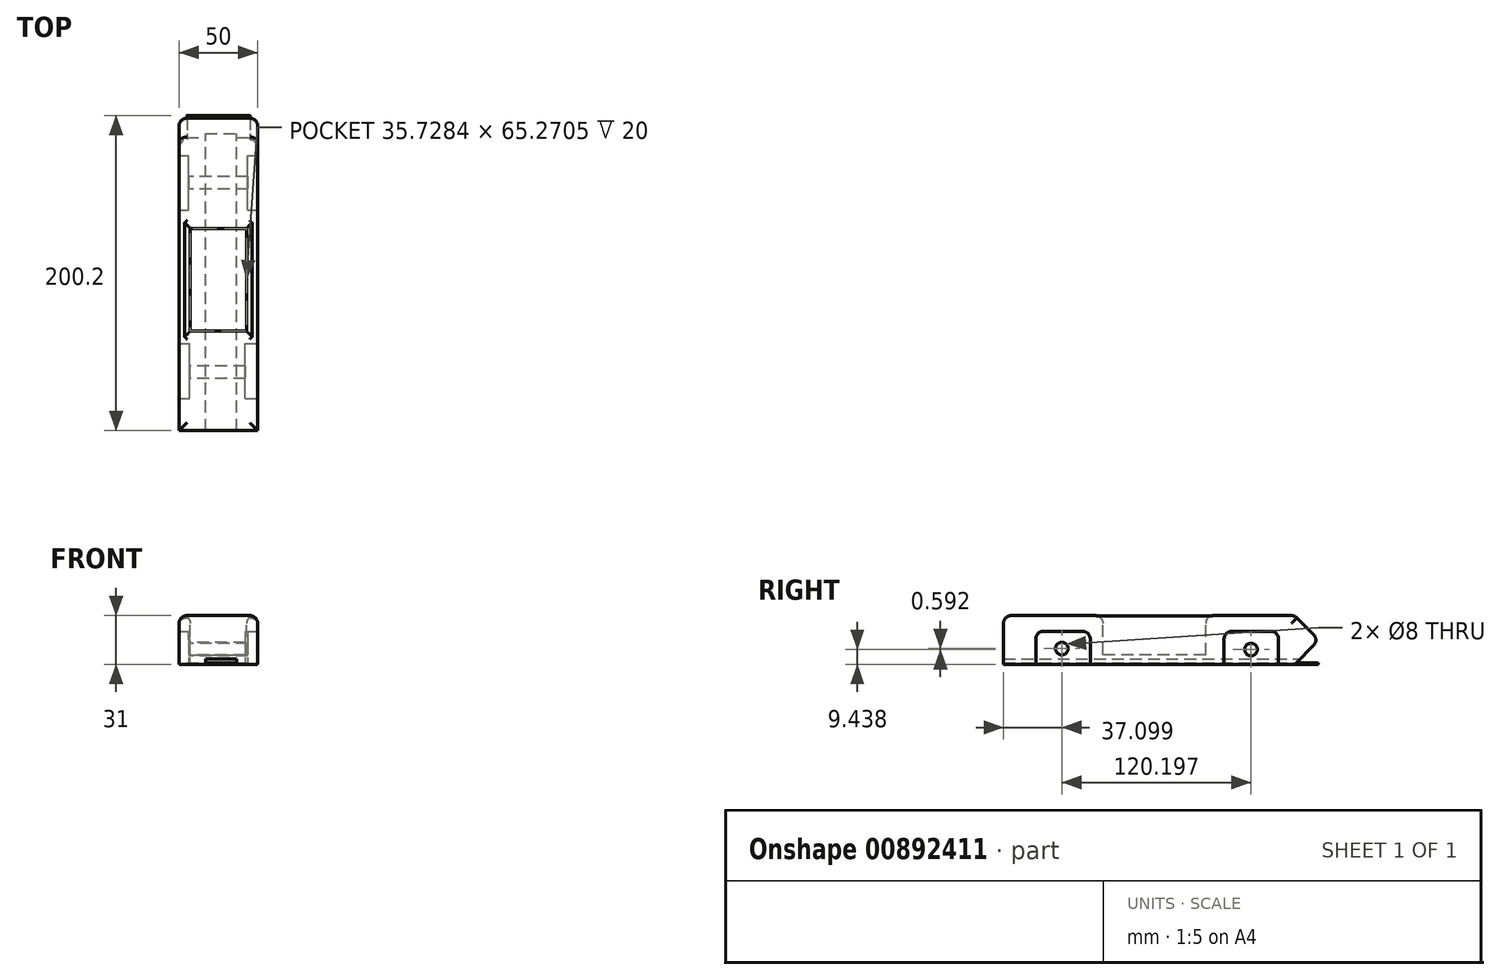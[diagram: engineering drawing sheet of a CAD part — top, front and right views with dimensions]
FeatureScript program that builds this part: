
annotation { "Feature Type Name" : "Feature", "Feature Type Description" : "" }
export const myFeature = defineFeature(function(context is Context, id is Id, definition is map)
    precondition{}
    {
        {
            var Q0;
            Q0=qCreatedBy(makeId("Top.planeOp"),FACE);
            var sketch = newSketch(context, id + "F0", { "sketchPlane" : qUnion([Q0])});
            skLineSegment(sketch, "E0.bottom", {"start": v(-27.3, 144.8) * mm, "end": v(22.7, 144.8) * mm});
            skLineSegment(sketch, "E0.top", {"start": v(-27.3, -55.2) * mm, "end": v(22.7, -55.2) * mm});
            skLineSegment(sketch, "E0.left", {"start": v(-27.3, 144.8) * mm, "end": v(-27.3, -55.2) * mm});
            skLineSegment(sketch, "E0.right", {"start": v(22.7, 144.8) * mm, "end": v(22.7, -55.2) * mm});
            skSolve(sketch);
        }
        {
            var Q0;
            Q0=makeQuery(id+"F0.imprint","IMPRINT",FACE,{"disambiguationData":[TD([[makeQuery(id+"F0.imprint","IMPRINT",EDGE,{"derivedFrom":sQuery(id+"F0.wireOp",EDGE,"E0.bottom")}),-1.0]])]});
            extrude(context, id + "F1", {"entities" : qUnion([Q0]), "depth" : 25 * mm, "offsetDistance" : 25 * mm});
        }
        {
            var Q0;
            Q0=makeQuery(id+"F1.opExtrude","CAP_FACE",FACE,{"disambiguationData":[OSD([sQuery(id+"F0.wireOp",EDGE,"E0.bottom"),sQuery(id+"F0.wireOp",EDGE,"E0.top"),sQuery(id+"F0.wireOp",EDGE,"E0.left"),sQuery(id+"F0.wireOp",EDGE,"E0.right")])],"isStart":true});
            var sketch = newSketch(context, id + "F2", { "sketchPlane" : qUnion([Q0])});
            skLineSegment(sketch, "E1.bottom", {"start": v(-27.3, -119.58) * mm, "end": v(22.7, -119.58) * mm});
            skLineSegment(sketch, "E1.top", {"start": v(-27.3, 34.65) * mm, "end": v(22.7, 34.65) * mm});
            skLineSegment(sketch, "E1.left", {"start": v(-27.3, -119.58) * mm, "end": v(-27.3, 34.65) * mm});
            skLineSegment(sketch, "E1.right", {"start": v(22.7, -119.58) * mm, "end": v(22.7, 34.65) * mm});
            skLineSegment(sketch, "E2.bottom", {"start": v(-27.3, -84.94) * mm, "end": v(22.7, -84.94) * mm});
            skLineSegment(sketch, "E2.top", {"start": v(-27.3, 0) * mm, "end": v(22.7, 0) * mm});
            skLineSegment(sketch, "E2.left", {"start": v(-27.3, -84.94) * mm, "end": v(-27.3, 0) * mm});
            skLineSegment(sketch, "E2.right", {"start": v(22.7, -84.94) * mm, "end": v(22.7, 0) * mm});
            skSolve(sketch);
        }
        {
            var Q0;
            {var subQ0=sQuery(id+"F2.wireOp",EDGE,"E1.top");Q0=makeQuery(id+"F2.imprint","IMPRINT",FACE,{"disambiguationData":[TD([[makeQuery(id+"F2.imprint","IMPRINT",EDGE,{"derivedFrom":subQ0}),-1.0]])]});}
            var sketch = newSketch(context, id + "F3", { "sketchPlane" : qUnion([Q0])});
            skLineSegment(sketch, "E3.top", {"start": v(-20.6, -127.1) * mm, "end": v(14.97, -127.1) * mm});
            skLineSegment(sketch, "E3.left", {"start": v(-20.6, 37.33) * mm, "end": v(-20.6, -127.1) * mm});
            skLineSegment(sketch, "E3.right", {"start": v(14.97, 37.33) * mm, "end": v(14.97, -127.1) * mm});
            skSolve(sketch);
        }
        {
            var Q0;
            {var subQ0=sQuery(id+"F2.wireOp",EDGE,"E1.top");Q0=makeQuery(id+"F2.imprint","IMPRINT",FACE,{"disambiguationData":[TD([[makeQuery(id+"F2.imprint","IMPRINT",EDGE,{"derivedFrom":subQ0}),-1.0]])]});}
            var sketch = newSketch(context, id + "F4", { "sketchPlane" : qUnion([Q0])});
            skLineSegment(sketch, "E4.bottom", {"start": v(-20.38, 34.74) * mm, "end": v(14.77, 34.74) * mm});
            skLineSegment(sketch, "E4.top", {"start": v(-20.38, 0) * mm, "end": v(14.77, 0) * mm});
            skLineSegment(sketch, "E4.left", {"start": v(-20.38, 34.74) * mm, "end": v(-20.38, 0) * mm});
            skLineSegment(sketch, "E4.right", {"start": v(14.77, 34.74) * mm, "end": v(14.77, 0) * mm});
            skSolve(sketch);
        }
        {
            var Q0;
            {var subQ0=sQuery(id+"F4.wireOp",EDGE,"E4.right");var subQ4=sQuery(id+"F2.wireOp",EDGE,"E1.top");var subQ5=makeQuery(id+"F2.imprint","IMPRINT",EDGE,{"derivedFrom":subQ4});var subQ6=makeQuery(id+"F4.imprint","INTERSECT",VERTEX,{"derivedFrom":[subQ5,subQ0]});Q0=makeQuery(id+"F4.imprint","IMPRINT",FACE,{"disambiguationData":[TD([[makeQuery(id+"F4.imprint","IMPRINT",EDGE,{"disambiguationData":[TD([[subQ6,-1.0]])],"derivedFrom":subQ0}),1.0]])]});}
            extrude(context, id + "F5", {"entities" : qUnion([Q0]), "operationType" : NewBodyOperationType.REMOVE, "oppositeDirection" : true, "depth" : 20 * mm, "offsetDistance" : 25 * mm});
        }
        {
            var Q0;
            {var subQ0=sQuery(id+"F3.wireOp",EDGE,"E3.left");var subQ1=sQuery(id+"F2.wireOp",EDGE,"E1.top");var subQ2=makeQuery(id+"F2.imprint","IMPRINT",EDGE,{"derivedFrom":subQ1});var subQ3=makeQuery(id+"F3.imprint","INTERSECT",VERTEX,{"derivedFrom":[subQ2,subQ0]});Q0=makeQuery(id+"F3.imprint","IMPRINT",FACE,{"disambiguationData":[TD([[makeQuery(id+"F3.imprint","IMPRINT",EDGE,{"disambiguationData":[TD([[subQ3,-1.0]])],"derivedFrom":subQ0}),-1.0]])]});}
            extrude(context, id + "F6", {"entities" : qUnion([Q0]), "operationType" : NewBodyOperationType.REMOVE, "oppositeDirection" : true, "depth" : 20 * mm, "offsetDistance" : 25 * mm});
        }
        {
            var Q0;
            {var subQ0=sQuery(id+"F2.wireOp",EDGE,"E1.bottom");Q0=makeQuery(id+"F2.imprint","IMPRINT",FACE,{"disambiguationData":[TD([[makeQuery(id+"F2.imprint","IMPRINT",EDGE,{"derivedFrom":subQ0}),1.0]])]});}
            var sketch = newSketch(context, id + "F7", { "sketchPlane" : qUnion([Q0])});
            skLineSegment(sketch, "E5.bottom", {"start": v(-21.28, -84.83) * mm, "end": v(16.36, -84.83) * mm});
            skLineSegment(sketch, "E5.top", {"start": v(-21.28, -119.98) * mm, "end": v(16.36, -119.98) * mm});
            skLineSegment(sketch, "E5.left", {"start": v(-21.28, -84.83) * mm, "end": v(-21.28, -119.98) * mm});
            skLineSegment(sketch, "E5.right", {"start": v(16.36, -84.83) * mm, "end": v(16.36, -119.98) * mm});
            skSolve(sketch);
        }
        {
            var Q0;
            {var subQ0=sQuery(id+"F7.wireOp",EDGE,"E5.left");var subQ1=sQuery(id+"F2.wireOp",EDGE,"E2.bottom");var subQ2=makeQuery(id+"F2.imprint","IMPRINT",EDGE,{"derivedFrom":subQ1});var subQ3=makeQuery(id+"F7.imprint","INTERSECT",VERTEX,{"derivedFrom":[subQ2,subQ0]});Q0=makeQuery(id+"F7.imprint","IMPRINT",FACE,{"disambiguationData":[TD([[makeQuery(id+"F7.imprint","IMPRINT",EDGE,{"disambiguationData":[TD([[subQ3,-1.0]])],"derivedFrom":subQ0}),-1.0]])]});}
            var Q1;
            {var subQ0=sQuery(id+"F7.wireOp",EDGE,"E5.right");var subQ1=sQuery(id+"F2.wireOp",EDGE,"E2.bottom");var subQ2=makeQuery(id+"F2.imprint","IMPRINT",EDGE,{"derivedFrom":subQ1});var subQ3=makeQuery(id+"F7.imprint","INTERSECT",VERTEX,{"derivedFrom":[subQ2,subQ0]});Q1=makeQuery(id+"F7.imprint","IMPRINT",FACE,{"disambiguationData":[TD([[makeQuery(id+"F7.imprint","IMPRINT",EDGE,{"disambiguationData":[TD([[subQ3,-1.0]])],"derivedFrom":subQ0}),1.0]])]});}
            extrude(context, id + "F8", {"entities" : qUnion([Q0, Q1]), "operationType" : NewBodyOperationType.REMOVE, "oppositeDirection" : true, "depth" : 20 * mm, "offsetDistance" : 25 * mm});
        }
        {
            var Q0;
            {var subQ0=sQuery(id+"F2.wireOp",EDGE,"E2.bottom");var subQ1=makeQuery(id+"F2.imprint","IMPRINT",EDGE,{"derivedFrom":subQ0});Q0=makeQuery(id+"F8.boolean.opBoolean","COPY",EDGE,{"derivedFrom":makeQuery(id+"F8.opExtrude","CAP_EDGE",EDGE,{"disambiguationData":[OSD([subQ0]),TDD([makeQuery(id+"F7.imprint","IMPRINT",EDGE,{"disambiguationData":[TD([[makeQuery(id+"F7.imprint","INTERSECT",VERTEX,{"derivedFrom":[subQ1,sQuery(id+"F7.wireOp",EDGE,"E5.right")]}),-1.0]])],"derivedFrom":subQ1})])],"isStart":false})});}
            var Q1;
            {var subQ1=sQuery(id+"F2.wireOp",EDGE,"E1.bottom");var subQ2=makeQuery(id+"F2.imprint","IMPRINT",EDGE,{"derivedFrom":subQ1});Q1=makeQuery(id+"F8.boolean.opBoolean","COPY",EDGE,{"derivedFrom":makeQuery(id+"F8.opExtrude","CAP_EDGE",EDGE,{"disambiguationData":[OSD([subQ1]),TDD([makeQuery(id+"F7.imprint","IMPRINT",EDGE,{"disambiguationData":[TD([[makeQuery(id+"F7.imprint","INTERSECT",VERTEX,{"derivedFrom":[subQ2,sQuery(id+"F7.wireOp",EDGE,"E5.right")]}),-1.0]])],"derivedFrom":subQ2})])],"isStart":false})});}
            var Q2;
            {var subQ1=sQuery(id+"F2.wireOp",EDGE,"E1.bottom");var subQ2=makeQuery(id+"F2.imprint","IMPRINT",EDGE,{"derivedFrom":subQ1});Q2=makeQuery(id+"F8.boolean.opBoolean","COPY",EDGE,{"derivedFrom":makeQuery(id+"F8.opExtrude","CAP_EDGE",EDGE,{"disambiguationData":[OSD([subQ1]),TDD([makeQuery(id+"F7.imprint","IMPRINT",EDGE,{"disambiguationData":[TD([[makeQuery(id+"F7.imprint","INTERSECT",VERTEX,{"derivedFrom":[subQ2,sQuery(id+"F7.wireOp",EDGE,"E5.left")]}),1.0]])],"derivedFrom":subQ2})])],"isStart":false})});}
            var Q3;
            {var subQ0=sQuery(id+"F2.wireOp",EDGE,"E2.bottom");var subQ1=makeQuery(id+"F2.imprint","IMPRINT",EDGE,{"derivedFrom":subQ0});Q3=makeQuery(id+"F8.boolean.opBoolean","COPY",EDGE,{"derivedFrom":makeQuery(id+"F8.opExtrude","CAP_EDGE",EDGE,{"disambiguationData":[OSD([subQ0]),TDD([makeQuery(id+"F7.imprint","IMPRINT",EDGE,{"disambiguationData":[TD([[makeQuery(id+"F7.imprint","INTERSECT",VERTEX,{"derivedFrom":[subQ1,sQuery(id+"F7.wireOp",EDGE,"E5.left")]}),1.0]])],"derivedFrom":subQ1})])],"isStart":false})});}
            fillet(context, id + "F9", {"entities" : qUnion([Q0, Q1, Q2, Q3]), "radius" : 5 * mm, "tangentPropagation" : true, "allowEdgeOverflow" : false});
        }
        {
            var Q0;
            Q0=makeQuery(id+"F6.boolean.opBoolean","COPY",EDGE,{"derivedFrom":makeQuery(id+"F6.opExtrude","CAP_EDGE",EDGE,{"disambiguationData":[OSD([sQuery(id+"F2.wireOp",EDGE,"E2.top")])],"isStart":false})});
            var Q1;
            Q1=makeQuery(id+"F5.boolean.opBoolean","COPY",EDGE,{"derivedFrom":makeQuery(id+"F5.opExtrude","CAP_EDGE",EDGE,{"disambiguationData":[OSD([sQuery(id+"F2.wireOp",EDGE,"E2.top")])],"isStart":false})});
            var Q2;
            Q2=makeQuery(id+"F5.boolean.opBoolean","COPY",EDGE,{"derivedFrom":makeQuery(id+"F5.opExtrude","CAP_EDGE",EDGE,{"disambiguationData":[OSD([sQuery(id+"F2.wireOp",EDGE,"E1.top")])],"isStart":false})});
            var Q3;
            Q3=makeQuery(id+"F6.boolean.opBoolean","COPY",EDGE,{"derivedFrom":makeQuery(id+"F6.opExtrude","CAP_EDGE",EDGE,{"disambiguationData":[OSD([sQuery(id+"F2.wireOp",EDGE,"E1.top")])],"isStart":false})});
            fillet(context, id + "F10", {"entities" : qUnion([Q0, Q1, Q2, Q3]), "radius" : 5 * mm, "tangentPropagation" : true, "allowEdgeOverflow" : false});
        }
        {
            var Q0;
            Q0=makeQuery(id+"F1.opExtrude","CAP_FACE",FACE,{"disambiguationData":[OSD([sQuery(id+"F0.wireOp",EDGE,"E0.bottom"),sQuery(id+"F0.wireOp",EDGE,"E0.top"),sQuery(id+"F0.wireOp",EDGE,"E0.left"),sQuery(id+"F0.wireOp",EDGE,"E0.right")])],"isStart":false});
            extrude(context, id + "F11", {"entities" : qUnion([Q0]), "operationType" : NewBodyOperationType.ADD, "depth" : 5 * mm, "offsetDistance" : 25 * mm});
        }
        {
            var Q0;
            Q0=makeQuery(id+"F11.opExtrude","CAP_EDGE",EDGE,{"disambiguationData":[OSD([sQuery(id+"F0.wireOp",EDGE,"E0.bottom")])],"isStart":false});
            chamfer(context, id + "F12", {"entities" : qUnion([Q0]), "width" : 15 * mm, "tangentPropagation" : true});
        }
        {
            var Q0;
            {var subQ0=sQuery(id+"F0.wireOp",EDGE,"E0.left");Q0=makeQuery(id+"F12.opChamfer","BLEND_EDGE",EDGE,{"blendedFrom":[makeQuery(id+"F11.opExtrude","CAP_EDGE",EDGE,{"disambiguationData":[OSD([sQuery(id+"F0.wireOp",EDGE,"E0.bottom")])],"isStart":false}),makeQuery(id+"F11.boolean.opBoolean","MERGE",FACE,{"derivedFrom":[makeQuery(id+"F1.opExtrude","SWEPT_FACE",FACE,{"disambiguationData":[OSD([subQ0])]}),makeQuery(id+"F11.opExtrude","SWEPT_FACE",FACE,{"disambiguationData":[OSD([subQ0])]})]})],"blendedInto":[makeQuery(id+"F11.boolean.opBoolean","MERGE",FACE,{"derivedFrom":[makeQuery(id+"F1.opExtrude","SWEPT_FACE",FACE,{"disambiguationData":[OSD([subQ0])]}),makeQuery(id+"F11.opExtrude","SWEPT_FACE",FACE,{"disambiguationData":[OSD([subQ0])]})]})]});}
            var Q1;
            Q1=makeQuery(id+"FpgZdjczDAoG9a3_1.opChamfer","BLEND_EDGE",EDGE,{"blendedFrom":[makeQuery(id+"F1.opExtrude","CAP_EDGE",EDGE,{"disambiguationData":[OSD([sQuery(id+"F0.wireOp",EDGE,"E0.bottom")])],"isStart":true}),makeQuery(id+"F1.opExtrude","SWEPT_FACE",FACE,{"disambiguationData":[OSD([sQuery(id+"F0.wireOp",EDGE,"E0.left")])]})],"blendedInto":[makeQuery(id+"F1.opExtrude","SWEPT_FACE",FACE,{"disambiguationData":[OSD([sQuery(id+"F0.wireOp",EDGE,"E0.left")])]})]});
            var Q2;
            {var subQ0=sQuery(id+"F0.wireOp",EDGE,"E0.right");Q2=makeQuery(id+"F12.opChamfer","BLEND_EDGE",EDGE,{"blendedFrom":[makeQuery(id+"F11.opExtrude","CAP_EDGE",EDGE,{"disambiguationData":[OSD([sQuery(id+"F0.wireOp",EDGE,"E0.bottom")])],"isStart":false}),makeQuery(id+"F11.boolean.opBoolean","MERGE",FACE,{"derivedFrom":[makeQuery(id+"F1.opExtrude","SWEPT_FACE",FACE,{"disambiguationData":[OSD([subQ0])]}),makeQuery(id+"F11.opExtrude","SWEPT_FACE",FACE,{"disambiguationData":[OSD([subQ0])]})]})],"blendedInto":[makeQuery(id+"F11.boolean.opBoolean","MERGE",FACE,{"derivedFrom":[makeQuery(id+"F1.opExtrude","SWEPT_FACE",FACE,{"disambiguationData":[OSD([subQ0])]}),makeQuery(id+"F11.opExtrude","SWEPT_FACE",FACE,{"disambiguationData":[OSD([subQ0])]})]})]});}
            var Q3;
            Q3=makeQuery(id+"FpgZdjczDAoG9a3_1.opChamfer","BLEND_EDGE",EDGE,{"blendedFrom":[makeQuery(id+"F1.opExtrude","CAP_EDGE",EDGE,{"disambiguationData":[OSD([sQuery(id+"F0.wireOp",EDGE,"E0.bottom")])],"isStart":true}),makeQuery(id+"F1.opExtrude","SWEPT_FACE",FACE,{"disambiguationData":[OSD([sQuery(id+"F0.wireOp",EDGE,"E0.right")])]})],"blendedInto":[makeQuery(id+"F1.opExtrude","SWEPT_FACE",FACE,{"disambiguationData":[OSD([sQuery(id+"F0.wireOp",EDGE,"E0.right")])]})]});
            fillet(context, id + "F13", {"entities" : qUnion([Q0, Q1, Q2, Q3]), "radius" : 5 * mm, "tangentPropagation" : true, "allowEdgeOverflow" : false});
        }
        {
            var Q0;
            {var subQ0=sQuery(id+"F2.wireOp",EDGE,"E1.bottom");Q0=makeQuery(id+"F2.imprint","IMPRINT",FACE,{"disambiguationData":[TD([[makeQuery(id+"F2.imprint","IMPRINT",EDGE,{"derivedFrom":subQ0}),-1.0]])]});}
            extrude(context, id + "F14", {"entities" : qUnion([Q0]), "operationType" : NewBodyOperationType.ADD, "depth" : 1 * mm, "offsetDistance" : 25 * mm});
        }
        {
            var Q0;
            Q0=makeQuery(id+"F1.opExtrude","CAP_FACE",FACE,{"disambiguationData":[OSD([sQuery(id+"F0.wireOp",EDGE,"E0.bottom"),sQuery(id+"F0.wireOp",EDGE,"E0.top"),sQuery(id+"F0.wireOp",EDGE,"E0.left"),sQuery(id+"F0.wireOp",EDGE,"E0.right")])],"isStart":true});
            extrude(context, id + "F15", {"entities" : qUnion([Q0]), "operationType" : NewBodyOperationType.ADD, "depth" : 2 * mm, "offsetDistance" : 25 * mm});
        }
        {
            var Q0;
            Q0=makeQuery(id+"F15.opExtrude","CAP_FACE",FACE,{"disambiguationData":[OSD([sQuery(id+"F0.wireOp",EDGE,"E0.bottom"),sQuery(id+"F0.wireOp",EDGE,"E0.top"),sQuery(id+"F0.wireOp",EDGE,"E0.left"),sQuery(id+"F0.wireOp",EDGE,"E0.right")])],"isStart":false});
            extrude(context, id + "F16", {"entities" : qUnion([Q0]), "operationType" : NewBodyOperationType.REMOVE, "oppositeDirection" : true, "depth" : 1 * mm, "offsetDistance" : 25 * mm});
        }
        {
            var Q0;
            Q0=makeQuery(id+"F11.opExtrude","CAP_FACE",FACE,{"disambiguationData":[OSD([sQuery(id+"F0.wireOp",EDGE,"E0.bottom"),sQuery(id+"F0.wireOp",EDGE,"E0.top"),sQuery(id+"F0.wireOp",EDGE,"E0.left"),sQuery(id+"F0.wireOp",EDGE,"E0.right")])],"isStart":false});
            var sketch = newSketch(context, id + "F17", { "sketchPlane" : qUnion([Q0])});
            skLineSegment(sketch, "E6.bottom", {"start": v(-20.1, 73.27) * mm, "end": v(15.62, 73.27) * mm});
            skLineSegment(sketch, "E6.top", {"start": v(-20.1, 8) * mm, "end": v(15.62, 8) * mm});
            skLineSegment(sketch, "E6.left", {"start": v(-20.1, 73.27) * mm, "end": v(-20.1, 8) * mm});
            skLineSegment(sketch, "E6.right", {"start": v(15.62, 73.27) * mm, "end": v(15.62, 8) * mm});
            skSolve(sketch);
        }
        {
            var Q0;
            Q0=makeQuery(id+"F17.imprint","IMPRINT",FACE,{"disambiguationData":[TD([[makeQuery(id+"F17.imprint","IMPRINT",EDGE,{"derivedFrom":sQuery(id+"F17.wireOp",EDGE,"E6.bottom")}),-1.0]])]});
            extrude(context, id + "F18", {"entities" : qUnion([Q0]), "operationType" : NewBodyOperationType.REMOVE, "oppositeDirection" : true, "depth" : 25 * mm, "offsetDistance" : 25 * mm});
        }
        {
            var Q0;
            {var subQ0=sQuery(id+"F7.wireOp",EDGE,"E5.left");Q0=makeQuery(id+"F15.boolean.opBoolean","MERGE",FACE,{"derivedFrom":[makeQuery(id+"F8.boolean.opBoolean","COPY",FACE,{"derivedFrom":makeQuery(id+"F8.opExtrude","SWEPT_FACE",FACE,{"disambiguationData":[OSD([subQ0])]})}),makeQuery(id+"F15.opExtrude","SWEPT_FACE",FACE,{"disambiguationData":[OSD([subQ0])]})]});}
            var sketch = newSketch(context, id + "F19", { "sketchPlane" : qUnion([Q0])});
            skCircle(sketch, "E7", {"center": v(-102.1, 8.44) * mm, "radius": 4 * mm});
            skCircle(sketch, "E8", {"center": v(18.1, 9.03) * mm, "radius": 4 * mm});
            skSolve(sketch);
        }
        {
            var Q0;
            Q0=makeQuery(id+"F19.imprint","IMPRINT",FACE,{"disambiguationData":[TD([[makeQuery(id+"F19.imprint","IMPRINT",EDGE,{"derivedFrom":sQuery(id+"F19.wireOp",EDGE,"E7")}),1.0]])]});
            var Q1;
            Q1=makeQuery(id+"F19.imprint","IMPRINT",FACE,{"disambiguationData":[TD([[makeQuery(id+"F19.imprint","IMPRINT",EDGE,{"derivedFrom":sQuery(id+"F19.wireOp",EDGE,"E8")}),1.0]])]});
            extrude(context, id + "F20", {"entities" : qUnion([Q0, Q1]), "operationType" : NewBodyOperationType.ADD, "depth" : 20 * mm, "offsetDistance" : 25 * mm});
        }
        {
            var Q0;
            {var subQ0=sQuery(id+"F0.wireOp",EDGE,"E0.bottom");Q0=makeQuery(id+"F14.boolean.opBoolean","MERGE",FACE,{"derivedFrom":[makeQuery(id+"F11.boolean.opBoolean","MERGE",FACE,{"derivedFrom":[makeQuery(id+"F1.opExtrude","SWEPT_FACE",FACE,{"disambiguationData":[OSD([subQ0])]}),makeQuery(id+"F11.opExtrude","SWEPT_FACE",FACE,{"disambiguationData":[OSD([subQ0])]})]}),makeQuery(id+"F14.opExtrude","SWEPT_FACE",FACE,{"disambiguationData":[OSD([subQ0])]})]});}
            var sketch = newSketch(context, id + "F21", { "sketchPlane" : qUnion([Q0])});
            skLineSegment(sketch, "E9.bottom", {"start": v(-9.33, 2.52) * mm, "end": v(10.5, 2.52) * mm});
            skLineSegment(sketch, "E9.top", {"start": v(-9.33, 0) * mm, "end": v(10.5, 0) * mm});
            skLineSegment(sketch, "E9.left", {"start": v(-9.33, 2.52) * mm, "end": v(-9.33, 0) * mm});
            skLineSegment(sketch, "E9.right", {"start": v(10.5, 2.52) * mm, "end": v(10.5, 0) * mm});
            skSolve(sketch);
        }
        {
            var Q0;
            Q0=makeQuery(id+"F21.imprint","IMPRINT",FACE,{"disambiguationData":[TD([[makeQuery(id+"F21.imprint","IMPRINT",EDGE,{"derivedFrom":sQuery(id+"F21.wireOp",EDGE,"E9.bottom")}),-1.0]])]});
            extrude(context, id + "F22", {"entities" : qUnion([Q0]), "operationType" : NewBodyOperationType.REMOVE, "oppositeDirection" : true, "depth" : 228 * mm, "offsetDistance" : 25 * mm});
        }
        {
            var Q0;
            Q0=makeQuery(id+"F14.opExtrude","CAP_EDGE",EDGE,{"disambiguationData":[OSD([sQuery(id+"F0.wireOp",EDGE,"E0.bottom")])],"isStart":false});
            chamfer(context, id + "F23", {"entities" : qUnion([Q0]), "width" : 15 * mm, "tangentPropagation" : true});
        }
        {
            var Q0;
            {var subQ0=sQuery(id+"F0.wireOp",EDGE,"E0.right");var subQ1=sQuery(id+"F0.wireOp",EDGE,"E0.top");var subQ2=sQuery(id+"F0.wireOp",EDGE,"E0.bottom");var subQ4=makeQuery(id+"F5.opExtrude","SWEPT_FACE",FACE,{"disambiguationData":[OSD([sQuery(id+"F2.wireOp",EDGE,"E2.top")])]});var subQ5=makeQuery(id+"F1.opExtrude","SWEPT_FACE",FACE,{"disambiguationData":[OSD([subQ0])]});var subQ9=makeQuery(id+"F1.opExtrude","CAP_EDGE",EDGE,{"disambiguationData":[OSD([subQ0])],"isStart":true});Q0=makeQuery(id+"F23.opChamfer","BLEND_EDGE",EDGE,{"blendedFrom":[makeQuery(id+"F14.opExtrude","CAP_EDGE",EDGE,{"disambiguationData":[OSD([subQ2])],"isStart":false}),makeQuery(id+"F15.boolean.opBoolean","MERGE",FACE,{"derivedFrom":[makeQuery(id+"F14.boolean.opBoolean","MERGE",FACE,{"derivedFrom":[makeQuery(id+"F11.boolean.opBoolean","MERGE",FACE,{"derivedFrom":[subQ5,makeQuery(id+"F11.opExtrude","SWEPT_FACE",FACE,{"disambiguationData":[OSD([subQ0])]})]}),makeQuery(id+"F14.opExtrude","SWEPT_FACE",FACE,{"disambiguationData":[OSD([subQ0])]})]}),makeQuery(id+"F15.opExtrude","SWEPT_FACE",FACE,{"disambiguationData":[OSD([subQ0]),TDD([makeQuery(id+"F5.boolean.opBoolean","SPLIT",EDGE,{"disambiguationData":[TD([makeQuery(id+"F1.opExtrude","SWEPT_FACE",FACE,{"disambiguationData":[OSD([subQ1])]})])],"derivedFrom":subQ9})])]}),makeQuery(id+"F15.opExtrude","SWEPT_FACE",FACE,{"disambiguationData":[OSD([subQ0]),TDD([makeQuery(id+"F8.boolean.opBoolean","SPLIT",EDGE,{"disambiguationData":[TD([makeQuery(id+"F5.boolean.opBoolean","COPY",FACE,{"derivedFrom":subQ4})])],"derivedFrom":makeQuery(id+"F5.boolean.opBoolean","SPLIT",EDGE,{"disambiguationData":[TD([makeQuery(id+"F1.opExtrude","SWEPT_FACE",FACE,{"disambiguationData":[OSD([subQ2])]})])],"derivedFrom":subQ9})})])]})]})],"blendedInto":[makeQuery(id+"F15.boolean.opBoolean","MERGE",FACE,{"derivedFrom":[makeQuery(id+"F14.boolean.opBoolean","MERGE",FACE,{"derivedFrom":[makeQuery(id+"F11.boolean.opBoolean","MERGE",FACE,{"derivedFrom":[subQ5,makeQuery(id+"F11.opExtrude","SWEPT_FACE",FACE,{"disambiguationData":[OSD([subQ0])]})]}),makeQuery(id+"F14.opExtrude","SWEPT_FACE",FACE,{"disambiguationData":[OSD([subQ0])]})]}),makeQuery(id+"F15.opExtrude","SWEPT_FACE",FACE,{"disambiguationData":[OSD([subQ0]),TDD([makeQuery(id+"F5.boolean.opBoolean","SPLIT",EDGE,{"disambiguationData":[TD([makeQuery(id+"F1.opExtrude","SWEPT_FACE",FACE,{"disambiguationData":[OSD([subQ1])]})])],"derivedFrom":subQ9})])]}),makeQuery(id+"F15.opExtrude","SWEPT_FACE",FACE,{"disambiguationData":[OSD([subQ0]),TDD([makeQuery(id+"F8.boolean.opBoolean","SPLIT",EDGE,{"disambiguationData":[TD([makeQuery(id+"F5.boolean.opBoolean","COPY",FACE,{"derivedFrom":subQ4})])],"derivedFrom":makeQuery(id+"F5.boolean.opBoolean","SPLIT",EDGE,{"disambiguationData":[TD([makeQuery(id+"F1.opExtrude","SWEPT_FACE",FACE,{"disambiguationData":[OSD([subQ2])]})])],"derivedFrom":subQ9})})])]})]})]});}
            var Q1;
            {var subQ0=sQuery(id+"F0.wireOp",EDGE,"E0.left");var subQ1=sQuery(id+"F0.wireOp",EDGE,"E0.top");var subQ2=sQuery(id+"F0.wireOp",EDGE,"E0.bottom");var subQ4=makeQuery(id+"F1.opExtrude","SWEPT_FACE",FACE,{"disambiguationData":[OSD([subQ0])]});var subQ5=makeQuery(id+"F6.opExtrude","SWEPT_FACE",FACE,{"disambiguationData":[OSD([sQuery(id+"F2.wireOp",EDGE,"E2.top")])]});var subQ9=makeQuery(id+"F1.opExtrude","CAP_EDGE",EDGE,{"disambiguationData":[OSD([subQ0])],"isStart":true});Q1=makeQuery(id+"F23.opChamfer","BLEND_EDGE",EDGE,{"blendedFrom":[makeQuery(id+"F14.opExtrude","CAP_EDGE",EDGE,{"disambiguationData":[OSD([subQ2])],"isStart":false}),makeQuery(id+"F15.boolean.opBoolean","MERGE",FACE,{"derivedFrom":[makeQuery(id+"F14.boolean.opBoolean","MERGE",FACE,{"derivedFrom":[makeQuery(id+"F11.boolean.opBoolean","MERGE",FACE,{"derivedFrom":[subQ4,makeQuery(id+"F11.opExtrude","SWEPT_FACE",FACE,{"disambiguationData":[OSD([subQ0])]})]}),makeQuery(id+"F14.opExtrude","SWEPT_FACE",FACE,{"disambiguationData":[OSD([subQ0])]})]}),makeQuery(id+"F15.opExtrude","SWEPT_FACE",FACE,{"disambiguationData":[OSD([subQ0]),TDD([makeQuery(id+"F6.boolean.opBoolean","SPLIT",EDGE,{"disambiguationData":[TD([makeQuery(id+"F1.opExtrude","SWEPT_FACE",FACE,{"disambiguationData":[OSD([subQ1])]})])],"derivedFrom":subQ9})])]}),makeQuery(id+"F15.opExtrude","SWEPT_FACE",FACE,{"disambiguationData":[OSD([subQ0]),TDD([makeQuery(id+"F8.boolean.opBoolean","SPLIT",EDGE,{"disambiguationData":[TD([makeQuery(id+"F6.boolean.opBoolean","COPY",FACE,{"derivedFrom":subQ5})])],"derivedFrom":makeQuery(id+"F6.boolean.opBoolean","SPLIT",EDGE,{"disambiguationData":[TD([makeQuery(id+"F1.opExtrude","SWEPT_FACE",FACE,{"disambiguationData":[OSD([subQ2])]})])],"derivedFrom":subQ9})})])]})]})],"blendedInto":[makeQuery(id+"F15.boolean.opBoolean","MERGE",FACE,{"derivedFrom":[makeQuery(id+"F14.boolean.opBoolean","MERGE",FACE,{"derivedFrom":[makeQuery(id+"F11.boolean.opBoolean","MERGE",FACE,{"derivedFrom":[subQ4,makeQuery(id+"F11.opExtrude","SWEPT_FACE",FACE,{"disambiguationData":[OSD([subQ0])]})]}),makeQuery(id+"F14.opExtrude","SWEPT_FACE",FACE,{"disambiguationData":[OSD([subQ0])]})]}),makeQuery(id+"F15.opExtrude","SWEPT_FACE",FACE,{"disambiguationData":[OSD([subQ0]),TDD([makeQuery(id+"F6.boolean.opBoolean","SPLIT",EDGE,{"disambiguationData":[TD([makeQuery(id+"F1.opExtrude","SWEPT_FACE",FACE,{"disambiguationData":[OSD([subQ1])]})])],"derivedFrom":subQ9})])]}),makeQuery(id+"F15.opExtrude","SWEPT_FACE",FACE,{"disambiguationData":[OSD([subQ0]),TDD([makeQuery(id+"F8.boolean.opBoolean","SPLIT",EDGE,{"disambiguationData":[TD([makeQuery(id+"F6.boolean.opBoolean","COPY",FACE,{"derivedFrom":subQ5})])],"derivedFrom":makeQuery(id+"F6.boolean.opBoolean","SPLIT",EDGE,{"disambiguationData":[TD([makeQuery(id+"F1.opExtrude","SWEPT_FACE",FACE,{"disambiguationData":[OSD([subQ2])]})])],"derivedFrom":subQ9})})])]})]})]});}
            fillet(context, id + "F24", {"entities" : qUnion([Q0, Q1]), "radius" : 5 * mm, "tangentPropagation" : true, "allowEdgeOverflow" : false});
        }
        {
            var Q0;
            {var subQ0=sQuery(id+"F0.wireOp",EDGE,"E0.right");var subQ1=sQuery(id+"F0.wireOp",EDGE,"E0.left");var subQ2=sQuery(id+"F0.wireOp",EDGE,"E0.bottom");Q0=makeQuery(id+"F16.boolean.opBoolean","MERGE",FACE,{"derivedFrom":[makeQuery(id+"F14.opExtrude","CAP_FACE",FACE,{"disambiguationData":[OSD([subQ2,subQ1,subQ0,sQuery(id+"F2.wireOp",EDGE,"E1.bottom")])],"isStart":false})],"fromTools":[makeQuery(id+"F16.opExtrude","CAP_FACE",FACE,{"disambiguationData":[OSD([subQ2,sQuery(id+"F0.wireOp",EDGE,"E0.top"),subQ1,subQ0])],"isStart":false})]});}
            extrude(context, id + "F25", {"entities" : qUnion([Q0]), "operationType" : NewBodyOperationType.ADD, "depth" : 1 * mm, "offsetDistance" : 25 * mm});
        }
        {
            var Q0;
            {var subQ0=sQuery(id+"F0.wireOp",EDGE,"E0.right");var subQ1=sQuery(id+"F0.wireOp",EDGE,"E0.left");var subQ2=sQuery(id+"F0.wireOp",EDGE,"E0.top");var subQ3=sQuery(id+"F0.wireOp",EDGE,"E0.bottom");var subQ4=sQuery(id+"F2.wireOp",EDGE,"E1.bottom");Q0=makeQuery(id+"F25.opExtrude","SWEPT_FACE",FACE,{"disambiguationData":[OSD([subQ3,subQ2,subQ1,subQ0,subQ4]),TDD([makeQuery(id+"F23.opChamfer","BLEND_EDGE",EDGE,{"blendedFrom":[makeQuery(id+"F14.opExtrude","CAP_EDGE",EDGE,{"disambiguationData":[OSD([subQ3])],"isStart":false}),makeQuery(id+"F16.boolean.opBoolean","MERGE",FACE,{"derivedFrom":[makeQuery(id+"F14.opExtrude","CAP_FACE",FACE,{"disambiguationData":[OSD([subQ3,subQ1,subQ0,subQ4])],"isStart":false})],"fromTools":[makeQuery(id+"F16.opExtrude","CAP_FACE",FACE,{"disambiguationData":[OSD([subQ3,subQ2,subQ1,subQ0])],"isStart":false})]})],"blendedInto":[makeQuery(id+"F16.boolean.opBoolean","MERGE",FACE,{"derivedFrom":[makeQuery(id+"F14.opExtrude","CAP_FACE",FACE,{"disambiguationData":[OSD([subQ3,subQ1,subQ0,subQ4])],"isStart":false})],"fromTools":[makeQuery(id+"F16.opExtrude","CAP_FACE",FACE,{"disambiguationData":[OSD([subQ3,subQ2,subQ1,subQ0])],"isStart":false})]})]})])]});}
            extrude(context, id + "F26", {"entities" : qUnion([Q0]), "operationType" : NewBodyOperationType.ADD, "depth" : 15.2 * mm, "offsetDistance" : 25 * mm});
        }
        {
            var Q0;
            {var subQ0=sQuery(id+"F0.wireOp",EDGE,"E0.right");var subQ1=sQuery(id+"F0.wireOp",EDGE,"E0.left");var subQ2=sQuery(id+"F0.wireOp",EDGE,"E0.top");var subQ3=sQuery(id+"F0.wireOp",EDGE,"E0.bottom");var subQ4=sQuery(id+"F2.wireOp",EDGE,"E1.bottom");var subQ5=makeQuery(id+"F23.opChamfer","BLEND_EDGE",EDGE,{"blendedFrom":[makeQuery(id+"F14.opExtrude","CAP_EDGE",EDGE,{"disambiguationData":[OSD([subQ3])],"isStart":false}),makeQuery(id+"F16.boolean.opBoolean","MERGE",FACE,{"derivedFrom":[makeQuery(id+"F14.opExtrude","CAP_FACE",FACE,{"disambiguationData":[OSD([subQ3,subQ1,subQ0,subQ4])],"isStart":false})],"fromTools":[makeQuery(id+"F16.opExtrude","CAP_FACE",FACE,{"disambiguationData":[OSD([subQ3,subQ2,subQ1,subQ0])],"isStart":false})]})],"blendedInto":[makeQuery(id+"F16.boolean.opBoolean","MERGE",FACE,{"derivedFrom":[makeQuery(id+"F14.opExtrude","CAP_FACE",FACE,{"disambiguationData":[OSD([subQ3,subQ1,subQ0,subQ4])],"isStart":false})],"fromTools":[makeQuery(id+"F16.opExtrude","CAP_FACE",FACE,{"disambiguationData":[OSD([subQ3,subQ2,subQ1,subQ0])],"isStart":false})]})]});Q0=makeQuery(id+"F26.opExtrude","SWEPT_FACE",FACE,{"disambiguationData":[OSD([subQ3,subQ2,subQ1,subQ0,subQ4]),TDD([makeQuery(id+"F25.boolean.opBoolean","MERGE",EDGE,{"derivedFrom":[subQ5,makeQuery(id+"F25.opExtrude","CAP_EDGE",EDGE,{"disambiguationData":[OSD([subQ3,subQ2,subQ1,subQ0,subQ4]),TDD([subQ5])],"isStart":true})]})])]});}
            extrude(context, id + "F27", {"entities" : qUnion([Q0]), "operationType" : NewBodyOperationType.ADD, "depth" : 1 * mm, "offsetDistance" : 25 * mm});
        }
        {
            var Q0;
            {var subQ0=sQuery(id+"F0.wireOp",EDGE,"E0.right");var subQ1=sQuery(id+"F0.wireOp",EDGE,"E0.left");var subQ2=sQuery(id+"F0.wireOp",EDGE,"E0.top");var subQ3=sQuery(id+"F0.wireOp",EDGE,"E0.bottom");var subQ4=sQuery(id+"F2.wireOp",EDGE,"E1.bottom");Q0=makeQuery(id+"F26.boolean.opBoolean","MERGE",FACE,{"derivedFrom":[makeQuery(id+"F25.opExtrude","CAP_FACE",FACE,{"disambiguationData":[OSD([subQ3,subQ2,subQ1,subQ0,subQ4])],"isStart":false}),makeQuery(id+"F26.opExtrude","SWEPT_FACE",FACE,{"disambiguationData":[OSD([subQ3,subQ2,subQ1,subQ0,subQ4]),TDD([makeQuery(id+"F25.opExtrude","CAP_EDGE",EDGE,{"disambiguationData":[OSD([subQ3,subQ2,subQ1,subQ0,subQ4]),TDD([makeQuery(id+"F23.opChamfer","BLEND_EDGE",EDGE,{"blendedFrom":[makeQuery(id+"F14.opExtrude","CAP_EDGE",EDGE,{"disambiguationData":[OSD([subQ3])],"isStart":false}),makeQuery(id+"F16.boolean.opBoolean","MERGE",FACE,{"derivedFrom":[makeQuery(id+"F14.opExtrude","CAP_FACE",FACE,{"disambiguationData":[OSD([subQ3,subQ1,subQ0,subQ4])],"isStart":false})],"fromTools":[makeQuery(id+"F16.opExtrude","CAP_FACE",FACE,{"disambiguationData":[OSD([subQ3,subQ2,subQ1,subQ0])],"isStart":false})]})],"blendedInto":[makeQuery(id+"F16.boolean.opBoolean","MERGE",FACE,{"derivedFrom":[makeQuery(id+"F14.opExtrude","CAP_FACE",FACE,{"disambiguationData":[OSD([subQ3,subQ1,subQ0,subQ4])],"isStart":false})],"fromTools":[makeQuery(id+"F16.opExtrude","CAP_FACE",FACE,{"disambiguationData":[OSD([subQ3,subQ2,subQ1,subQ0])],"isStart":false})]})]})])],"isStart":false})])]})]});}
            extrude(context, id + "F28", {"entities" : qUnion([Q0]), "operationType" : NewBodyOperationType.REMOVE, "oppositeDirection" : true, "depth" : 1 * mm, "offsetDistance" : 25 * mm});
        }
        {
            var Q0;
            {var subQ0=sQuery(id+"F0.wireOp",EDGE,"E0.right");var subQ1=sQuery(id+"F0.wireOp",EDGE,"E0.left");var subQ2=sQuery(id+"F0.wireOp",EDGE,"E0.top");var subQ3=sQuery(id+"F0.wireOp",EDGE,"E0.bottom");var subQ4=sQuery(id+"F2.wireOp",EDGE,"E1.bottom");Q0=makeQuery(id+"F28.boolean.opBoolean","COPY",EDGE,{"derivedFrom":makeQuery(id+"F28.opExtrude","CAP_EDGE",EDGE,{"disambiguationData":[OSD([subQ3,subQ2,subQ1,subQ0,subQ4]),TDD([makeQuery(id+"F26.opExtrude","CAP_EDGE",EDGE,{"disambiguationData":[OSD([subQ3,subQ2,subQ1,subQ0,subQ4]),TDD([makeQuery(id+"F25.opExtrude","CAP_EDGE",EDGE,{"disambiguationData":[OSD([subQ3,subQ2,subQ1,subQ0,subQ4]),TDD([makeQuery(id+"F23.opChamfer","BLEND_EDGE",EDGE,{"blendedFrom":[makeQuery(id+"F14.opExtrude","CAP_EDGE",EDGE,{"disambiguationData":[OSD([subQ3])],"isStart":false}),makeQuery(id+"F16.boolean.opBoolean","MERGE",FACE,{"derivedFrom":[makeQuery(id+"F14.opExtrude","CAP_FACE",FACE,{"disambiguationData":[OSD([subQ3,subQ1,subQ0,subQ4])],"isStart":false})],"fromTools":[makeQuery(id+"F16.opExtrude","CAP_FACE",FACE,{"disambiguationData":[OSD([subQ3,subQ2,subQ1,subQ0])],"isStart":false})]})],"blendedInto":[makeQuery(id+"F16.boolean.opBoolean","MERGE",FACE,{"derivedFrom":[makeQuery(id+"F14.opExtrude","CAP_FACE",FACE,{"disambiguationData":[OSD([subQ3,subQ1,subQ0,subQ4])],"isStart":false})],"fromTools":[makeQuery(id+"F16.opExtrude","CAP_FACE",FACE,{"disambiguationData":[OSD([subQ3,subQ2,subQ1,subQ0])],"isStart":false})]})]})])],"isStart":false})])],"isStart":false})])],"isStart":false})});}
            var Q1;
            {var subQ0=sQuery(id+"F0.wireOp",EDGE,"E0.right");var subQ1=sQuery(id+"F0.wireOp",EDGE,"E0.left");var subQ2=sQuery(id+"F0.wireOp",EDGE,"E0.top");var subQ3=sQuery(id+"F0.wireOp",EDGE,"E0.bottom");var subQ4=sQuery(id+"F2.wireOp",EDGE,"E1.bottom");var subQ5=makeQuery(id+"F23.opChamfer","BLEND_EDGE",EDGE,{"blendedFrom":[makeQuery(id+"F14.opExtrude","CAP_EDGE",EDGE,{"disambiguationData":[OSD([subQ3])],"isStart":false}),makeQuery(id+"F16.boolean.opBoolean","MERGE",FACE,{"derivedFrom":[makeQuery(id+"F14.opExtrude","CAP_FACE",FACE,{"disambiguationData":[OSD([subQ3,subQ1,subQ0,subQ4])],"isStart":false})],"fromTools":[makeQuery(id+"F16.opExtrude","CAP_FACE",FACE,{"disambiguationData":[OSD([subQ3,subQ2,subQ1,subQ0])],"isStart":false})]})],"blendedInto":[makeQuery(id+"F16.boolean.opBoolean","MERGE",FACE,{"derivedFrom":[makeQuery(id+"F14.opExtrude","CAP_FACE",FACE,{"disambiguationData":[OSD([subQ3,subQ1,subQ0,subQ4])],"isStart":false})],"fromTools":[makeQuery(id+"F16.opExtrude","CAP_FACE",FACE,{"disambiguationData":[OSD([subQ3,subQ2,subQ1,subQ0])],"isStart":false})]})]});Q1=makeQuery(id+"F27.opExtrude","CAP_EDGE",EDGE,{"disambiguationData":[OSD([subQ3,subQ2,subQ1,subQ0,subQ4]),TDD([makeQuery(id+"F26.opExtrude","CAP_EDGE",EDGE,{"disambiguationData":[OSD([subQ3,subQ2,subQ1,subQ0,subQ4]),TDD([makeQuery(id+"F25.boolean.opBoolean","MERGE",EDGE,{"derivedFrom":[subQ5,makeQuery(id+"F25.opExtrude","CAP_EDGE",EDGE,{"disambiguationData":[OSD([subQ3,subQ2,subQ1,subQ0,subQ4]),TDD([subQ5])],"isStart":true})]})])],"isStart":false})])],"isStart":false});}
            fillet(context, id + "F29", {"entities" : qUnion([Q0, Q1]), "radius" : 1 * mm, "tangentPropagation" : true, "allowEdgeOverflow" : false});
        }
        {
            var Q0;
            Q0=makeQuery(id+"F11.opExtrude","CAP_EDGE",EDGE,{"disambiguationData":[OSD([sQuery(id+"F0.wireOp",EDGE,"E0.left")])],"isStart":false});
            var Q1;
            Q1=makeQuery(id+"F11.opExtrude","CAP_FACE",FACE,{"disambiguationData":[OSD([sQuery(id+"F0.wireOp",EDGE,"E0.bottom"),sQuery(id+"F0.wireOp",EDGE,"E0.top"),sQuery(id+"F0.wireOp",EDGE,"E0.left"),sQuery(id+"F0.wireOp",EDGE,"E0.right")])],"isStart":false});
            fillet(context, id + "F30", {"entities" : qUnion([Q0, Q1]), "radius" : 5 * mm, "tangentPropagation" : true, "allowEdgeOverflow" : false});
        }
        {
            var Q0;
            Q0=makeQuery(id+"F20.opExtrude","CAP_FACE",FACE,{"disambiguationData":[OSD([sQuery(id+"F19.wireOp",EDGE,"E7")])],"isStart":false});
            extrude(context, id + "F31", {"entities" : qUnion([Q0]), "operationType" : NewBodyOperationType.REMOVE, "oppositeDirection" : true, "depth" : 114 * mm, "offsetDistance" : 25 * mm});
        }
        {
            var Q0;
            Q0=makeQuery(id+"F20.opExtrude","CAP_FACE",FACE,{"disambiguationData":[OSD([sQuery(id+"F19.wireOp",EDGE,"E8")])],"isStart":false});
            extrude(context, id + "F32", {"entities" : qUnion([Q0]), "operationType" : NewBodyOperationType.REMOVE, "oppositeDirection" : true, "depth" : 113 * mm, "offsetDistance" : 25 * mm});
        }
        {
            var Q0;
            Q0=makeQuery(id+"F19.imprint","IMPRINT",FACE,{"disambiguationData":[TD([[makeQuery(id+"F19.imprint","IMPRINT",EDGE,{"derivedFrom":sQuery(id+"F19.wireOp",EDGE,"E8")}),1.0]])]});
            extrude(context, id + "F33", {"entities" : qUnion([Q0]), "operationType" : NewBodyOperationType.REMOVE, "oppositeDirection" : true, "depth" : 62.5 * mm, "offsetDistance" : 25 * mm});
        }
    });
